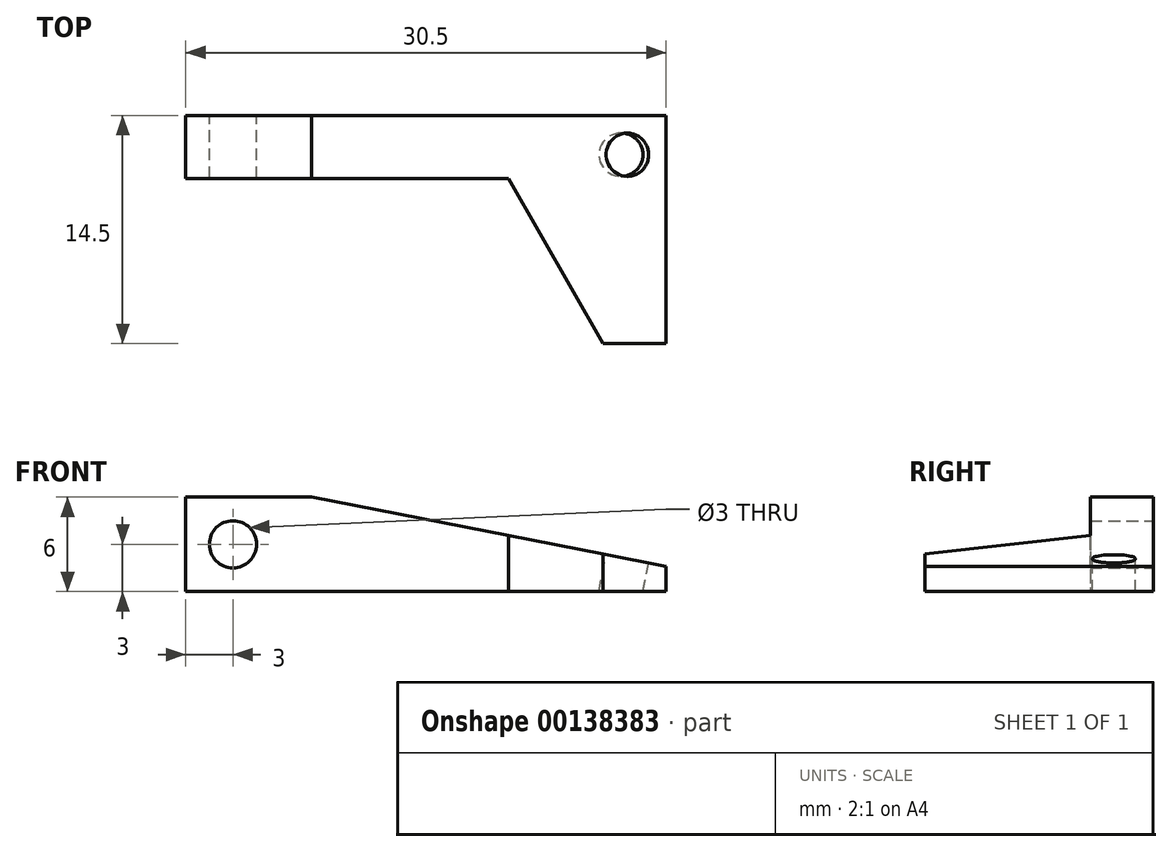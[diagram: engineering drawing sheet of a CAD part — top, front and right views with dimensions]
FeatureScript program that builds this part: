
annotation { "Feature Type Name" : "Feature", "Feature Type Description" : "" }
export const myFeature = defineFeature(function(context is Context, id is Id, definition is map)
    precondition{}
    {
        {
            var Q0;
            Q0=qCreatedBy(makeId("Front.planeOp"),FACE);
            var sketch = newSketch(context, id + "F0", { "sketchPlane" : qUnion([Q0])});
            skCircle(sketch, "E0", {"center": v(0, 0) * mm, "radius": 1.5 * mm});
            skLineSegment(sketch, "E1.bottom", {"start": v(-3, 3) * mm, "end": v(5, 3) * mm});
            skLineSegment(sketch, "E1.top", {"start": v(-3, -3) * mm, "end": v(27.5, -3) * mm});
            skLineSegment(sketch, "E1.left", {"start": v(-3, 3) * mm, "end": v(-3, -3) * mm});
            skLineSegment(sketch, "E1.right", {"start": v(27.5, -1.4) * mm, "end": v(27.5, -3) * mm});
            skLineSegment(sketch, "E2", {"start": v(0, 0) * mm, "end": v(-3, 0) * mm, "construction": true});
            skLineSegment(sketch, "E3", {"start": v(0, 0) * mm, "end": v(0, 3) * mm, "construction": true});
            skLineSegment(sketch, "E4", {"start": v(5, 3) * mm, "end": v(27.5, -1.4) * mm});
            skSolve(sketch);
        }
        {
            var Q0;
            Q0 = qSketchRegion(id + "F0", true);
            extrude(context, id + "F1", {"entities" : qUnion([Q0]), "depth" : 4 * mm});
        }
        {
            var Q0;
            Q0=makeQuery(id+"F1.opExtrude","CAP_FACE",FACE,{"disambiguationData":[OSD([sQuery(id+"F0.wireOp",EDGE,"E0"),sQuery(id+"F0.wireOp",EDGE,"E1.bottom"),sQuery(id+"F0.wireOp",EDGE,"E1.top"),sQuery(id+"F0.wireOp",EDGE,"E1.left"),sQuery(id+"F0.wireOp",EDGE,"E1.right"),sQuery(id+"F0.wireOp",EDGE,"E4")])],"isStart":false});
            var sketch = newSketch(context, id + "F2", { "sketchPlane" : qUnion([Q0])});
            skLineSegment(sketch, "E5", {"start": v(27.5, -3) * mm, "end": v(27.5, -1.4) * mm});
            skLineSegment(sketch, "E6", {"start": v(27.5, -1.4) * mm, "end": v(17.5, 0.56) * mm});
            skLineSegment(sketch, "E7", {"start": v(17.5, 0.56) * mm, "end": v(17.5, -3) * mm});
            skLineSegment(sketch, "E8", {"start": v(17.5, -3) * mm, "end": v(27.5, -3) * mm});
            skSolve(sketch);
        }
        {
            var Q0;
            Q0 = qSketchRegion(id + "F2", true);
            extrude(context, id + "F3", {"entities" : qUnion([Q0]), "operationType" : NewBodyOperationType.ADD, "depth" : 10.5 * mm});
        }
        {
            var Q0;
            Q0=makeQuery(id+"F3.boolean.opBoolean","MERGE",FACE,{"derivedFrom":[makeQuery(id+"F1.opExtrude","SWEPT_FACE",FACE,{"disambiguationData":[OSD([sQuery(id+"F0.wireOp",EDGE,"E1.top")])]}),makeQuery(id+"F3.opExtrude","SWEPT_FACE",FACE,{"disambiguationData":[OSD([sQuery(id+"F2.wireOp",EDGE,"E8")])]})]});
            var sketch = newSketch(context, id + "F4", { "sketchPlane" : qUnion([Q0])});
            skLineSegment(sketch, "E9", {"start": v(17.5, 14.5) * mm, "end": v(23.5, 14.5) * mm});
            skLineSegment(sketch, "E10", {"start": v(23.5, 14.5) * mm, "end": v(17.5, 4) * mm});
            skLineSegment(sketch, "E11", {"start": v(17.5, 4) * mm, "end": v(17.5, 14.5) * mm});
            skSolve(sketch);
        }
        {
            var Q0;
            Q0 = qSketchRegion(id + "F4", true);
            extrude(context, id + "F5", {"entities" : qUnion([Q0]), "operationType" : NewBodyOperationType.REMOVE, "endBound" : BoundingType.THROUGH_ALL, "oppositeDirection" : true, "depth" : 25 * mm});
        }
        {
            var Q0;
            Q0=makeQuery(id+"F3.boolean.opBoolean","MERGE",FACE,{"derivedFrom":[makeQuery(id+"F1.opExtrude","SWEPT_FACE",FACE,{"disambiguationData":[OSD([sQuery(id+"F0.wireOp",EDGE,"E4")])]}),makeQuery(id+"F3.opExtrude","SWEPT_FACE",FACE,{"disambiguationData":[OSD([sQuery(id+"F2.wireOp",EDGE,"E6")])]})]});
            var sketch = newSketch(context, id + "F6", { "sketchPlane" : qUnion([Q0])});
            skCircle(sketch, "E12", {"center": v(24.76, -2.5) * mm, "radius": 1.38 * mm});
            skLineSegment(sketch, "E13", {"start": v(24.76, -2.5) * mm, "end": v(27.26, -2.5) * mm, "construction": true});
            skLineSegment(sketch, "E14", {"start": v(24.76, -2.5) * mm, "end": v(24.76, 0) * mm, "construction": true});
            skSolve(sketch);
        }
        {
            var Q0;
            Q0 = qSketchRegion(id + "F6", true);
            extrude(context, id + "F7", {"entities" : qUnion([Q0]), "operationType" : NewBodyOperationType.REMOVE, "endBound" : BoundingType.THROUGH_ALL, "oppositeDirection" : true, "depth" : 25 * mm});
        }
    });
